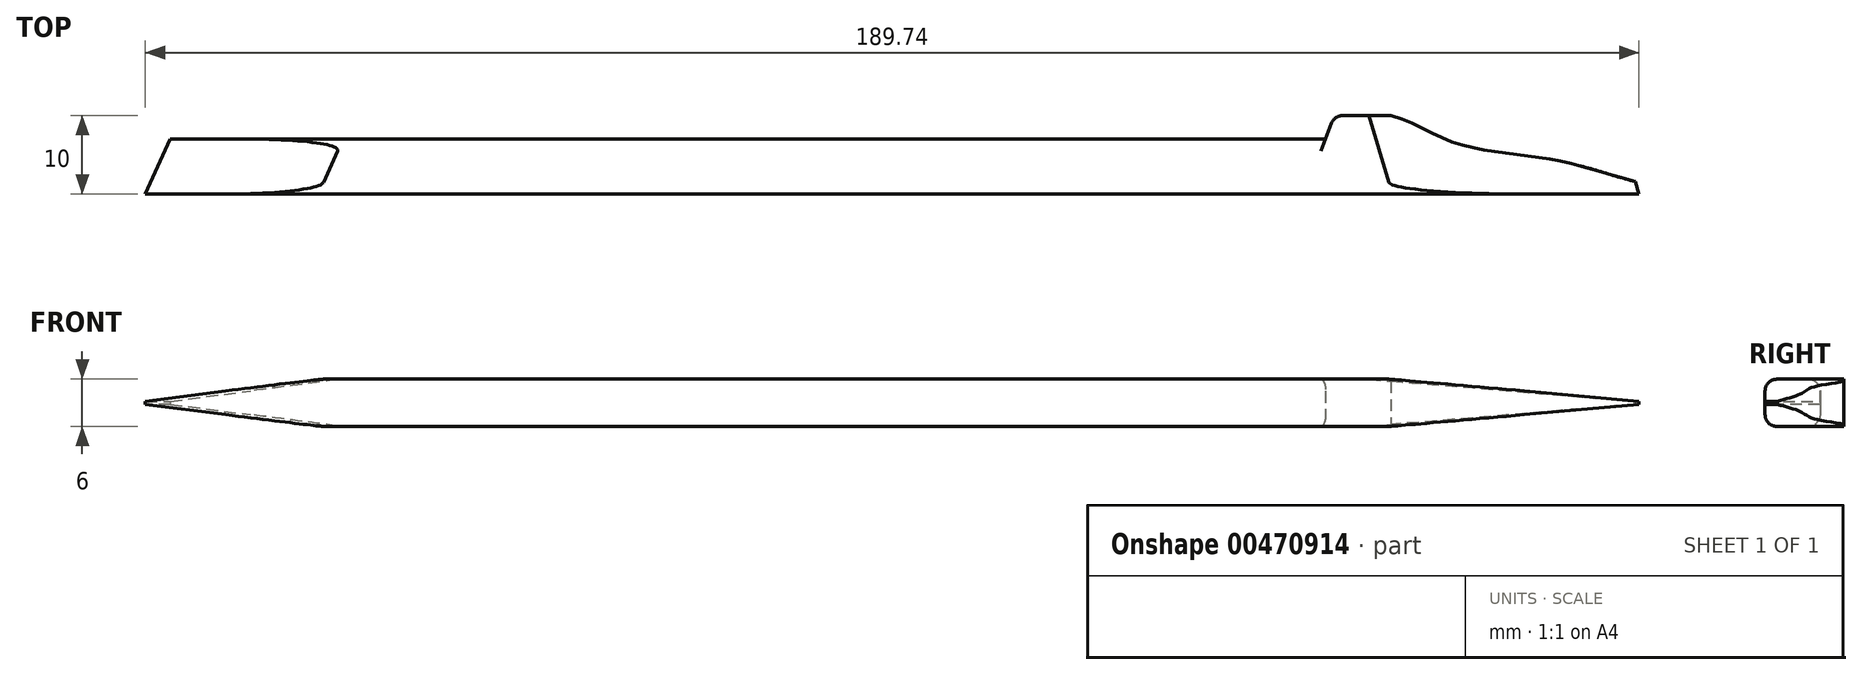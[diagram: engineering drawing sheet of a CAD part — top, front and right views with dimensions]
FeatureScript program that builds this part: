
annotation { "Feature Type Name" : "Feature", "Feature Type Description" : "" }
export const myFeature = defineFeature(function(context is Context, id is Id, definition is map)
    precondition{}
    {
        {
            var Q0;
            Q0=qCreatedBy(makeId("Top.planeOp"),FACE);
            var sketch = newSketch(context, id + "F0", { "sketchPlane" : qUnion([Q0])});
            skLineSegment(sketch, "E0", {"start": v(-81.83, 7) * mm, "end": v(38.17, 7) * mm});
            skLineSegment(sketch, "E1", {"start": v(38.17, 7) * mm, "end": v(39.3, 10) * mm});
            skLineSegment(sketch, "E2", {"start": v(39.3, 10) * mm, "end": v(46.5, 10) * mm});
            skLineSegment(sketch, "E3", {"start": v(-81.83, 7) * mm, "end": v(-81.83, 0) * mm});
            skLineSegment(sketch, "E4", {"start": v(-81.83, 0) * mm, "end": v(46.5, 0) * mm});
            skLineSegment(sketch, "E5", {"start": v(46.5, 0) * mm, "end": v(78, 0) * mm});
            skPoint(sketch, "E6", {"position": v(38.52, 0) * mm});
            skLineSegment(sketch, "E7", {"start": v(38.17, 7) * mm, "end": v(38.52, 0) * mm});
            skLineSegment(sketch, "E8", {"start": v(-81.83, 7) * mm, "end": v(-108.59, 7) * mm});
            skLineSegment(sketch, "E9", {"start": v(-108.59, 7) * mm, "end": v(-111.75, 0) * mm});
            skLineSegment(sketch, "E10", {"start": v(-111.75, 0) * mm, "end": v(-81.83, 0) * mm});
            skLineSegment(sketch, "E11", {"start": v(78, 0) * mm, "end": v(77.51, 1.59) * mm});
            skFitSpline(sketch, "E12", {"points": [v(46.5, 10) * mm, v(54.59, 6.52) * mm, v(67.12, 4.37) * mm, v(77.51, 1.59) * mm], "startDerivative": vector(30.48, -8.35) * mm, "endDerivative": vector(31.02, -8.25) * mm});
            skSolve(sketch);
        }
        {
            var Q0;
            Q0=makeQuery(id+"F0.imprint","IMPRINT",FACE,{"disambiguationData":[TD([[makeQuery(id+"F0.imprint","IMPRINT",EDGE,{"derivedFrom":sQuery(id+"F0.wireOp",EDGE,"E0")}),-1.0]])]});
            var Q1;
            Q1=makeQuery(id+"F0.imprint","IMPRINT",FACE,{"disambiguationData":[TD([[makeQuery(id+"F0.imprint","IMPRINT",EDGE,{"derivedFrom":sQuery(id+"F0.wireOp",EDGE,"E1")}),-1.0]])]});
            var Q2;
            Q2=makeQuery(id+"F0.imprint","IMPRINT",FACE,{"disambiguationData":[TD([[makeQuery(id+"F0.imprint","IMPRINT",EDGE,{"derivedFrom":sQuery(id+"F0.wireOp",EDGE,"E3")}),-1.0]])]});
            extrude(context, id + "F1", {"entities" : qUnion([Q0, Q1, Q2]), "depth" : 6 * mm});
        }
        {
            var Q0;
            Q0=makeQuery(id+"F1.opExtrude","CAP_EDGE",EDGE,{"disambiguationData":[OSD([sQuery(id+"F0.wireOp",EDGE,"E11")])],"isStart":false});
            var Q1;
            Q1=makeQuery(id+"F1.opExtrude","CAP_EDGE",EDGE,{"disambiguationData":[OSD([sQuery(id+"F0.wireOp",EDGE,"E11")])],"isStart":true});
            chamfer(context, id + "F2", {"entities" : qUnion([Q0, Q1]), "chamferType" : ChamferType.TWO_OFFSETS, "width1" : 30 * mm, "oppositeDirection" : false, "width2" : 2.8 * mm, "tangentPropagation" : true});
        }
        {
            var Q0;
            Q0=makeQuery(id+"F1.opExtrude","CAP_EDGE",EDGE,{"disambiguationData":[OSD([sQuery(id+"F0.wireOp",EDGE,"E0")])],"isStart":false});
            var Q1;
            Q1=makeQuery(id+"F1.opExtrude","CAP_EDGE",EDGE,{"disambiguationData":[OSD([sQuery(id+"F0.wireOp",EDGE,"E0")])],"isStart":true});
            var Q2;
            Q2=makeQuery(id+"F1.opExtrude","CAP_EDGE",EDGE,{"disambiguationData":[OSD([sQuery(id+"F0.wireOp",EDGE,"E4"),sQuery(id+"F0.wireOp",EDGE,"E5")])],"isStart":false});
            var Q3;
            Q3=makeQuery(id+"F1.opExtrude","CAP_EDGE",EDGE,{"disambiguationData":[OSD([sQuery(id+"F0.wireOp",EDGE,"E4"),sQuery(id+"F0.wireOp",EDGE,"E5")])],"isStart":true});
            var Q4;
            Q4=makeQuery(id+"F1.opExtrude","SWEPT_EDGE",EDGE,{"disambiguationData":[OSD([sQuery(id+"F0.wireOp",EDGE,"E1"),sQuery(id+"F0.wireOp",EDGE,"E2")])]});
            fillet(context, id + "F3", {"entities" : qUnion([Q0, Q1, Q2, Q3, Q4]), "radius" : 1.5 * mm, "tangentPropagation" : true, "allowEdgeOverflow" : false});
        }
        {
            var Q0;
            Q0=makeQuery(id+"F1.opExtrude","CAP_EDGE",EDGE,{"disambiguationData":[OSD([sQuery(id+"F0.wireOp",EDGE,"E9")])],"isStart":false});
            var Q1;
            Q1=makeQuery(id+"F1.opExtrude","CAP_EDGE",EDGE,{"disambiguationData":[OSD([sQuery(id+"F0.wireOp",EDGE,"E9")])],"isStart":true});
            chamfer(context, id + "F4", {"entities" : qUnion([Q0, Q1]), "chamferType" : ChamferType.TWO_OFFSETS, "width1" : 20 * mm, "oppositeDirection" : false, "width2" : 2.8 * mm});
        }
    });
